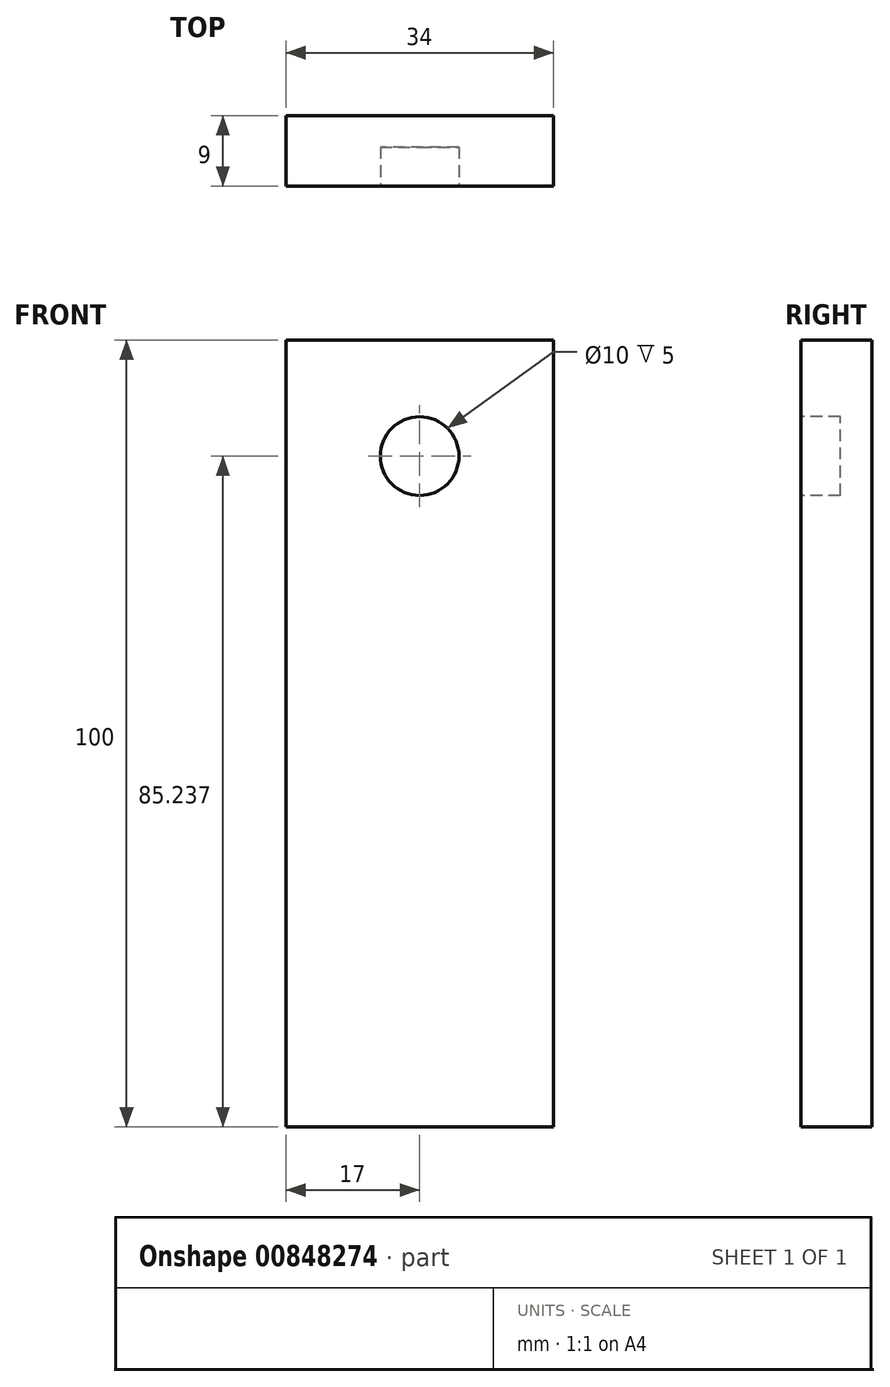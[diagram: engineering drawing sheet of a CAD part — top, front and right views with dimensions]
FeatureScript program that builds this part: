
annotation { "Feature Type Name" : "Feature", "Feature Type Description" : "" }
export const myFeature = defineFeature(function(context is Context, id is Id, definition is map)
    precondition{}
    {
        {
            var Q0;
            Q0=qCreatedBy(makeId("Top.planeOp"),FACE);
            var sketch = newSketch(context, id + "F0", { "sketchPlane" : qUnion([Q0])});
            skLineSegment(sketch, "E0.bottom", {"start": v(0, 0) * mm, "end": v(-34, 0) * mm});
            skLineSegment(sketch, "E0.top", {"start": v(0, 9) * mm, "end": v(-34, 9) * mm});
            skLineSegment(sketch, "E0.left", {"start": v(0, 0) * mm, "end": v(0, 9) * mm});
            skLineSegment(sketch, "E0.right", {"start": v(-34, 0) * mm, "end": v(-34, 9) * mm});
            skSolve(sketch);
        }
        {
            var Q0;
            Q0=makeQuery(id+"F0.imprint","IMPRINT",FACE,{"disambiguationData":[TD([[makeQuery(id+"F0.imprint","IMPRINT",EDGE,{"derivedFrom":sQuery(id+"F0.wireOp",EDGE,"E0.bottom")}),-1.0]])]});
            extrude(context, id + "F1", {"entities" : qUnion([Q0]), "depth" : 100 * mm, "offsetDistance" : 25 * mm});
        }
        {
            var Q0;
            Q0=makeQuery(id+"F1.opExtrude","SWEPT_FACE",FACE,{"disambiguationData":[OSD([sQuery(id+"F0.wireOp",EDGE,"E0.bottom")])]});
            var sketch = newSketch(context, id + "F2", { "sketchPlane" : qUnion([Q0])});
            skCircle(sketch, "E1", {"center": v(-17, 85.24) * mm, "radius": 5 * mm});
            skSolve(sketch);
        }
        {
            var Q0;
            Q0=makeQuery(id+"F2.imprint","IMPRINT",FACE,{"disambiguationData":[TD([[makeQuery(id+"F2.imprint","IMPRINT",EDGE,{"derivedFrom":sQuery(id+"F2.wireOp",EDGE,"E1")}),1.0]])]});
            extrude(context, id + "F3", {"entities" : qUnion([Q0]), "operationType" : NewBodyOperationType.REMOVE, "oppositeDirection" : true, "depth" : 5 * mm, "offsetDistance" : 25 * mm});
        }
    });
